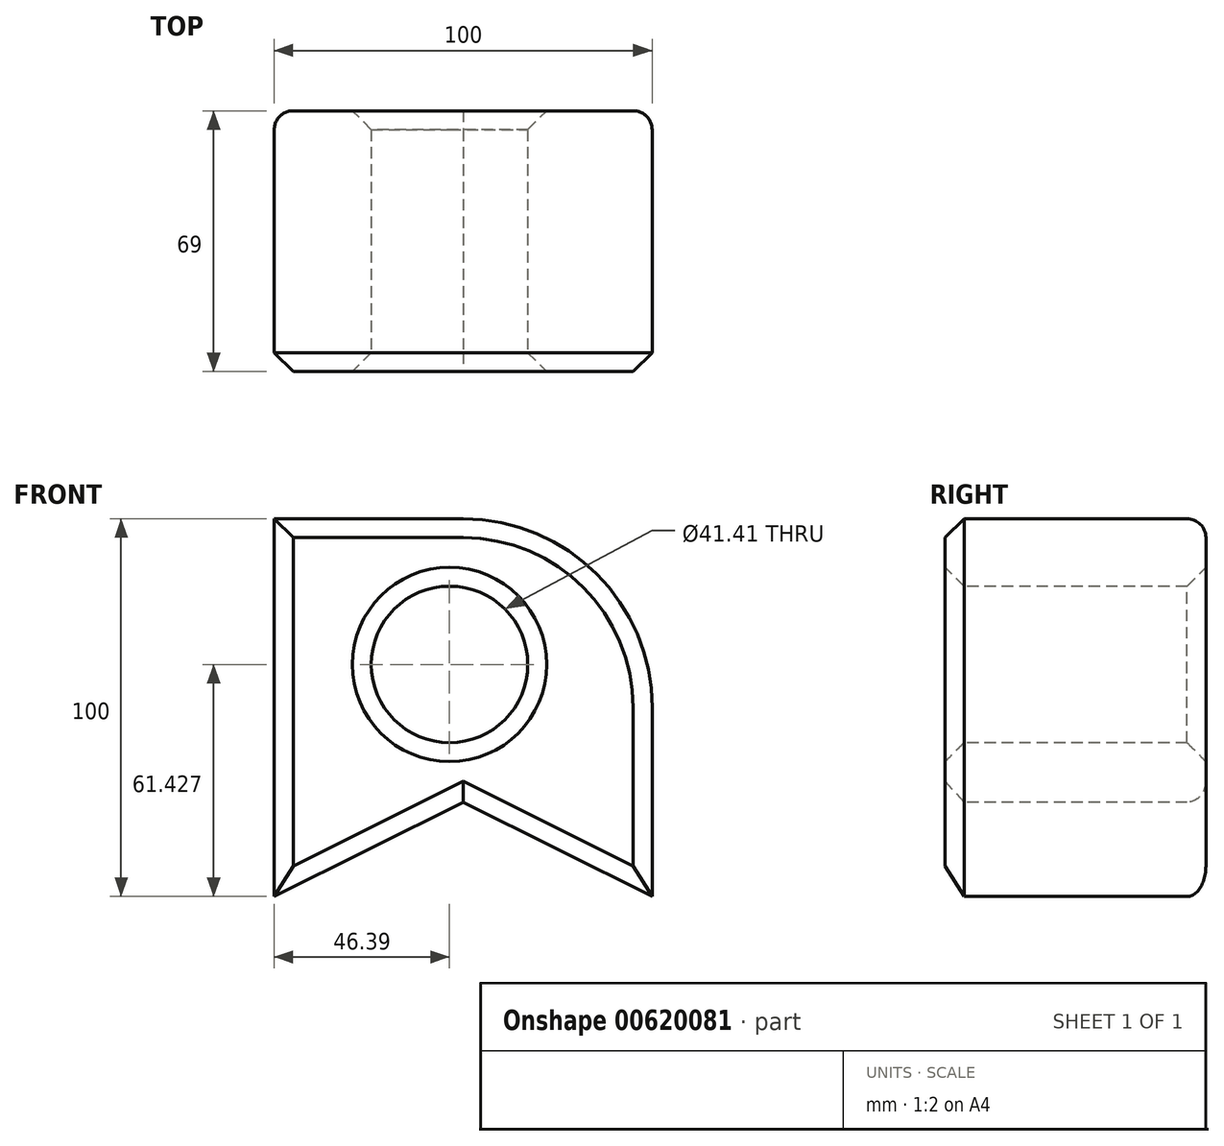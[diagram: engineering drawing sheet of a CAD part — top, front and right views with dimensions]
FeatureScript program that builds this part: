
annotation { "Feature Type Name" : "Feature", "Feature Type Description" : "" }
export const myFeature = defineFeature(function(context is Context, id is Id, definition is map)
    precondition{}
    {
        {
            var Q0;
            Q0=qCreatedBy(makeId("Front.planeOp"),FACE);
            var sketch = newSketch(context, id + "F0", { "sketchPlane" : qUnion([Q0])});
            skLineSegment(sketch, "E0.bottom", {"start": v(3.61, -46.11) * mm, "end": v(3.61, -46.11) * mm});
            skLineSegment(sketch, "E0.left", {"start": v(-46.39, -96.11) * mm, "end": v(-46.39, -146.11) * mm});
            skLineSegment(sketch, "E0.right", {"start": v(53.61, -96.11) * mm, "end": v(53.61, -146.11) * mm});
            skPoint(sketch, "E1.visualSharp", {"position": v(-46.39, -46.11) * mm});
            skPoint(sketch, "E2.visualSharp", {"position": v(53.61, -46.11) * mm});
            skArc(sketch, "E2.filletArc", {"start": v(53.61, -96.11) * mm, "mid": v(38.97, -60.76) * mm, "end": v(3.61, -46.11) * mm});
            skLineSegment(sketch, "E3", {"start": v(-46.39, -146.11) * mm, "end": v(3.61, -121.11) * mm});
            skLineSegment(sketch, "E4", {"start": v(3.61, -121.11) * mm, "end": v(53.61, -146.11) * mm});
            skLineSegment(sketch, "E5", {"start": v(-46.39, -96.11) * mm, "end": v(-46.39, -41.69) * mm});
            skLineSegment(sketch, "E6", {"start": v(-46.39, -46.11) * mm, "end": v(3.61, -46.11) * mm});
            skSolve(sketch);
        }
        {
            var Q0;
            Q0 = qSketchRegion(id + "F0", true);
            extrude(context, id + "F1", {"entities" : qUnion([Q0]), "oppositeDirection" : true, "depth" : 69 * mm, "offsetDistance" : 25 * mm});
        }
        {
            var Q0;
            Q0=makeQuery(id+"F1.opExtrude","CAP_FACE",FACE,{"disambiguationData":[OSD([sQuery(id+"F0.wireOp",EDGE,"E0.left"),sQuery(id+"F0.wireOp",EDGE,"E0.right"),sQuery(id+"F0.wireOp",EDGE,"E2.filletArc"),sQuery(id+"F0.wireOp",EDGE,"E3"),sQuery(id+"F0.wireOp",EDGE,"E4"),sQuery(id+"F0.wireOp",EDGE,"E5"),sQuery(id+"F0.wireOp",EDGE,"E6")])],"isStart":false});
            fillet(context, id + "F2", {"entities" : qUnion([Q0]), "radius" : 5 * mm, "tangentPropagation" : true, "allowEdgeOverflow" : false});
        }
        {
            var Q0;
            Q0=makeQuery(id+"F1.opExtrude","CAP_FACE",FACE,{"disambiguationData":[OSD([sQuery(id+"F0.wireOp",EDGE,"E0.left"),sQuery(id+"F0.wireOp",EDGE,"E0.right"),sQuery(id+"F0.wireOp",EDGE,"E2.filletArc"),sQuery(id+"F0.wireOp",EDGE,"E3"),sQuery(id+"F0.wireOp",EDGE,"E4"),sQuery(id+"F0.wireOp",EDGE,"E5"),sQuery(id+"F0.wireOp",EDGE,"E6")])],"isStart":true});
            chamfer(context, id + "F3", {"entities" : qUnion([Q0]), "width" : 5 * mm, "tangentPropagation" : true});
        }
        {
            var Q0;
            Q0=makeQuery(id+"F1.opExtrude","CAP_FACE",FACE,{"disambiguationData":[OSD([sQuery(id+"F0.wireOp",EDGE,"E0.left"),sQuery(id+"F0.wireOp",EDGE,"E0.right"),sQuery(id+"F0.wireOp",EDGE,"E2.filletArc"),sQuery(id+"F0.wireOp",EDGE,"E3"),sQuery(id+"F0.wireOp",EDGE,"E4"),sQuery(id+"F0.wireOp",EDGE,"E5"),sQuery(id+"F0.wireOp",EDGE,"E6")])],"isStart":true});
            var sketch = newSketch(context, id + "F4", { "sketchPlane" : qUnion([Q0])});
            skCircle(sketch, "E7", {"center": v(0, -84.68) * mm, "radius": 20.7 * mm});
            skSolve(sketch);
        }
        {
            var Q0;
            Q0=makeQuery(id+"F4.imprint","IMPRINT",FACE,{"disambiguationData":[TD([[makeQuery(id+"F4.imprint","IMPRINT",EDGE,{"derivedFrom":sQuery(id+"F4.wireOp",EDGE,"E7")}),1.0]])]});
            extrude(context, id + "F5", {"entities" : qUnion([Q0]), "operationType" : NewBodyOperationType.REMOVE, "oppositeDirection" : true, "depth" : 69 * mm, "offsetDistance" : 25 * mm});
        }
        {
            var Q0;
            Q0=makeQuery(id+"F5.boolean.opBoolean","COPY",FACE,{"derivedFrom":makeQuery(id+"F5.opExtrude","SWEPT_FACE",FACE,{"disambiguationData":[OSD([sQuery(id+"F4.wireOp",EDGE,"E7")])]})});
            chamfer(context, id + "F6", {"entities" : qUnion([Q0]), "width" : 5 * mm, "tangentPropagation" : true});
        }
    });
